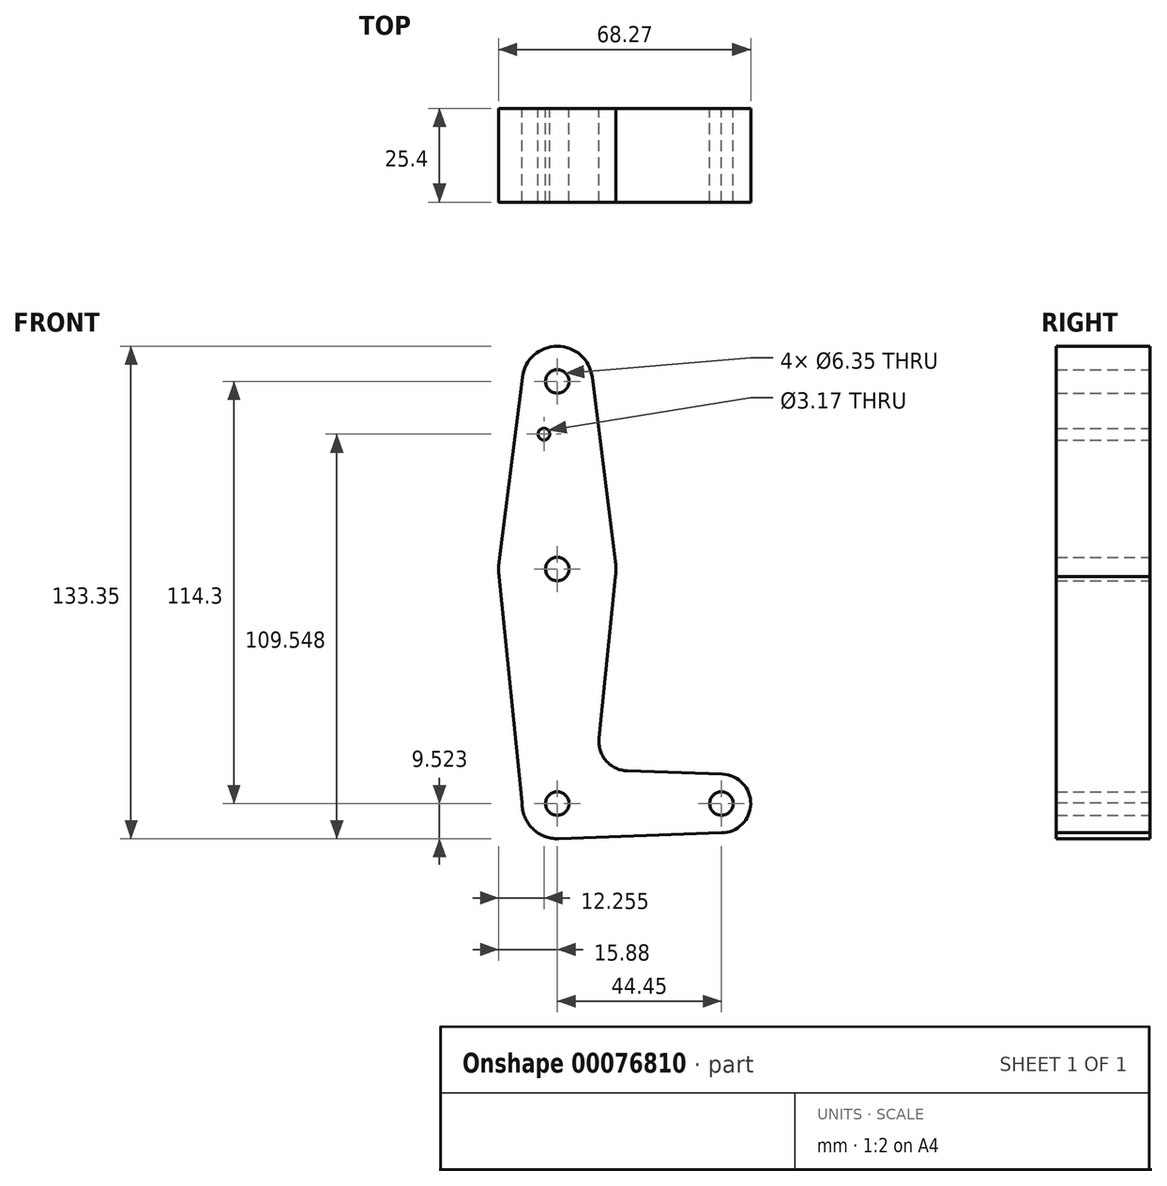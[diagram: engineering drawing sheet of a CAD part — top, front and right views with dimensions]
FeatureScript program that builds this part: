
annotation { "Feature Type Name" : "Feature", "Feature Type Description" : "" }
export const myFeature = defineFeature(function(context is Context, id is Id, definition is map)
    precondition{}
    {
        {
            var Q0;
            Q0=qCreatedBy(makeId("Front.planeOp"),FACE);
            var sketch = newSketch(context, id + "F0", { "sketchPlane" : qUnion([Q0])});
            skLineSegment(sketch, "E0", {"start": v(-44.45, 83.52) * mm, "end": v(-44.45, -30.78) * mm});
            skLineSegment(sketch, "E1", {"start": v(0, -30.78) * mm, "end": v(-44.45, -30.78) * mm});
            skCircle(sketch, "E2", {"center": v(-44.45, 83.52) * mm, "radius": 9.53 * mm});
            skCircle(sketch, "E3", {"center": v(-44.45, 32.72) * mm, "radius": 15.88 * mm});
            skCircle(sketch, "E4", {"center": v(-44.45, -30.78) * mm, "radius": 9.53 * mm});
            skCircle(sketch, "E5", {"center": v(0, -30.78) * mm, "radius": 7.94 * mm});
            skLineSegment(sketch, "E6", {"start": v(-53.97, -30.6) * mm, "end": v(-53.97, -30.6) * mm});
            skLineSegment(sketch, "E7", {"start": v(-53.9, 84.71) * mm, "end": v(-60.2, 34.7) * mm});
            skLineSegment(sketch, "E8", {"start": v(-60.2, 34.7) * mm, "end": v(-60.2, 30.74) * mm});
            skLineSegment(sketch, "E9", {"start": v(-60.2, 30.74) * mm, "end": v(-53.97, -30.6) * mm});
            skLineSegment(sketch, "E10", {"start": v(-35, 84.71) * mm, "end": v(-28.7, 34.7) * mm});
            skLineSegment(sketch, "E11", {"start": v(-28.7, 34.7) * mm, "end": v(-28.7, 30.74) * mm});
            skCircle(sketch, "E12", {"center": v(-48.07, 69.25) * mm, "radius": 1.59 * mm});
            skCircle(sketch, "E13", {"center": v(-44.45, 32.72) * mm, "radius": 3.18 * mm});
            skCircle(sketch, "E14", {"center": v(-44.45, 83.52) * mm, "radius": 3.18 * mm});
            skCircle(sketch, "E15", {"center": v(-44.45, -30.78) * mm, "radius": 3.18 * mm});
            skCircle(sketch, "E16", {"center": v(0, -30.78) * mm, "radius": 3.18 * mm});
            skLineSegment(sketch, "E17", {"start": v(-25.52, -21.93) * mm, "end": v(0.28, -22.84) * mm});
            skLineSegment(sketch, "E18", {"start": v(-33.14, -13.18) * mm, "end": v(-28.7, 30.74) * mm});
            skArc(sketch, "E19.filletArc", {"start": v(-33.14, -13.18) * mm, "mid": v(-31.23, -19.2) * mm, "end": v(-25.52, -21.93) * mm});
            skLineSegment(sketch, "E20", {"start": v(0, -38.71) * mm, "end": v(-44.1, -40.3) * mm});
            skSolve(sketch);
        }
        {
            var Q0;
            Q0 = qSketchRegion(id + "F0", true);
            var Q1;
            {var subQ0=sQuery(id+"F0.wireOp",EDGE,"E4");var subQ1=sQuery(id+"F0.wireOp",EDGE,"E0");var subQ2=makeQuery(id+"F0.imprint","INTERSECT",VERTEX,{"derivedFrom":[subQ1,subQ0]});Q1=makeQuery(id+"F0.imprint","IMPRINT",FACE,{"disambiguationData":[TD([[makeQuery(id+"F0.imprint","IMPRINT",EDGE,{"disambiguationData":[TD([[subQ2,-1.0]])],"derivedFrom":subQ1}),1.0]])]});}
            extrude(context, id + "F1", {"entities" : qUnion([Q0, Q1]), "depth" : 25.4 * mm});
        }
    });
